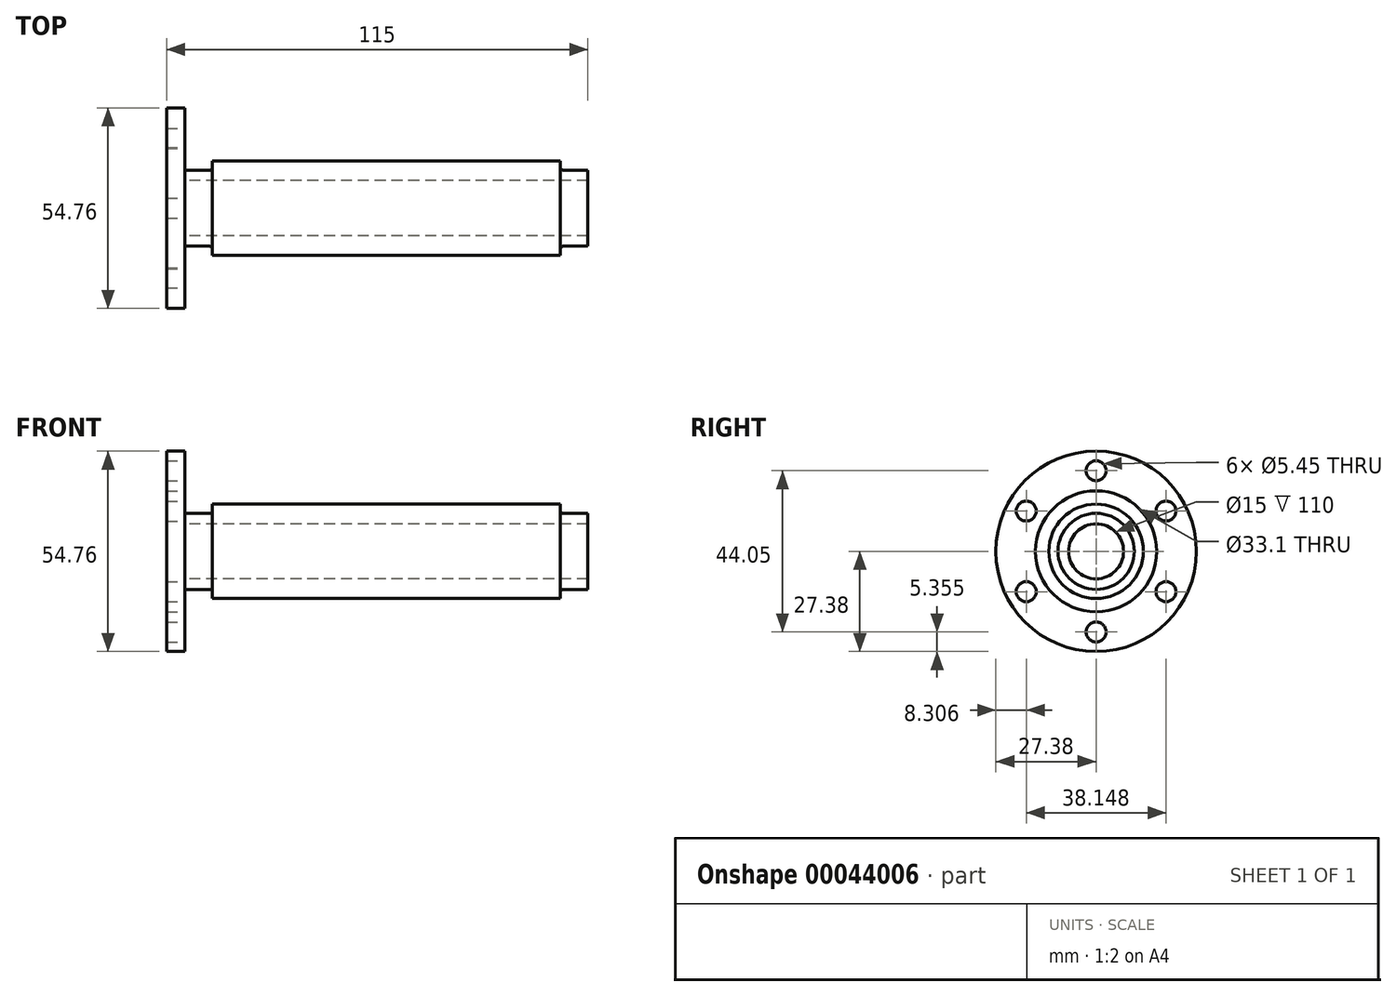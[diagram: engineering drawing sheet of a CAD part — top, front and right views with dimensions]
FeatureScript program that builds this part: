
annotation { "Feature Type Name" : "Feature", "Feature Type Description" : "" }
export const myFeature = defineFeature(function(context is Context, id is Id, definition is map)
    precondition{}
    {
        {
            var Q0;
            Q0=qCreatedBy(makeId("Front.planeOp"),FACE);
            var sketch = newSketch(context, id + "F0", { "sketchPlane" : qUnion([Q0])});
            skLineSegment(sketch, "E0", {"start": v(0, 0) * mm, "end": v(-45.87, 0) * mm});
            skLineSegment(sketch, "E1.0", {"start": v(0, 16.55) * mm, "end": v(-5, 16.55) * mm});
            skLineSegment(sketch, "E2.0", {"start": v(0, 27.38) * mm, "end": v(-5, 27.38) * mm});
            skLineSegment(sketch, "E3", {"start": v(0, 16.55) * mm, "end": v(0, 27.38) * mm});
            skLineSegment(sketch, "E4.0", {"start": v(-5, 16.55) * mm, "end": v(-5, 27.38) * mm});
            skSolve(sketch);
        }
        {
            var Q0;
            Q0=makeQuery(id+"F0.imprint","IMPRINT",FACE,{"disambiguationData":[TD([[makeQuery(id+"F0.imprint","IMPRINT",EDGE,{"derivedFrom":sQuery(id+"F0.wireOp",EDGE,"E1.0")}),-1.0]])]});
            var Q1;
            Q1=sQuery(id+"F0.wireOp",EDGE,"E0");
            revolve(context, id + "F1", {"entities" : qUnion([Q0]), "axis" : qUnion([Q1]), "revolveType" : RevolveType.FULL});
        }
        {
            var Q0;
            Q0=qCreatedBy(makeId("Right.planeOp"),FACE);
            var sketch = newSketch(context, id + "F2", { "sketchPlane" : qUnion([Q0])});
            skCircle(sketch, "E5", {"center": v(0, 22.02) * mm, "radius": 2.73 * mm});
            skCircle(sketch, "E6.1.0", {"center": v(-19.07, 11.01) * mm, "radius": 2.73 * mm});
            skCircle(sketch, "E6.2.0", {"center": v(-19.07, -11.01) * mm, "radius": 2.73 * mm});
            skCircle(sketch, "E6.3.0", {"center": v(0, -22.02) * mm, "radius": 2.73 * mm});
            skCircle(sketch, "E6.4.0", {"center": v(19.07, -11.01) * mm, "radius": 2.73 * mm});
            skCircle(sketch, "E6.5.0", {"center": v(19.07, 11.01) * mm, "radius": 2.73 * mm});
            skPoint(sketch, "E6.center", {"position": v(0, 0) * mm});
            skSolve(sketch);
        }
        {
            var Q0;
            Q0=makeQuery(id+"F2.imprint","IMPRINT",FACE,{"disambiguationData":[TD([[makeQuery(id+"F2.imprint","IMPRINT",EDGE,{"derivedFrom":sQuery(id+"F2.wireOp",EDGE,"E5")}),1.0]])]});
            var Q1;
            Q1=makeQuery(id+"F2.imprint","IMPRINT",FACE,{"disambiguationData":[TD([[makeQuery(id+"F2.imprint","IMPRINT",EDGE,{"derivedFrom":sQuery(id+"F2.wireOp",EDGE,"E6.1.0")}),1.0]])]});
            var Q2;
            Q2=makeQuery(id+"F2.imprint","IMPRINT",FACE,{"disambiguationData":[TD([[makeQuery(id+"F2.imprint","IMPRINT",EDGE,{"derivedFrom":sQuery(id+"F2.wireOp",EDGE,"E6.2.0")}),1.0]])]});
            var Q3;
            Q3=makeQuery(id+"F2.imprint","IMPRINT",FACE,{"disambiguationData":[TD([[makeQuery(id+"F2.imprint","IMPRINT",EDGE,{"derivedFrom":sQuery(id+"F2.wireOp",EDGE,"E6.3.0")}),1.0]])]});
            var Q4;
            Q4=makeQuery(id+"F2.imprint","IMPRINT",FACE,{"disambiguationData":[TD([[makeQuery(id+"F2.imprint","IMPRINT",EDGE,{"derivedFrom":sQuery(id+"F2.wireOp",EDGE,"E6.4.0")}),1.0]])]});
            var Q5;
            Q5=makeQuery(id+"F2.imprint","IMPRINT",FACE,{"disambiguationData":[TD([[makeQuery(id+"F2.imprint","IMPRINT",EDGE,{"derivedFrom":sQuery(id+"F2.wireOp",EDGE,"E6.5.0")}),1.0]])]});
            extrude(context, id + "F3", {"entities" : qUnion([Q0, Q1, Q2, Q3, Q4, Q5]), "operationType" : NewBodyOperationType.REMOVE, "oppositeDirection" : true, "depth" : 25 * mm});
        }
        {
            var Q0;
            Q0=qCreatedBy(makeId("Front.planeOp"),FACE);
            var sketch = newSketch(context, id + "F4", { "sketchPlane" : qUnion([Q0])});
            skLineSegment(sketch, "E7", {"start": v(6.15, 0) * mm, "end": v(138.41, 0) * mm});
            skLineSegment(sketch, "E8.bottom", {"start": v(0, 7.5) * mm, "end": v(110, 7.5) * mm});
            skLineSegment(sketch, "E8.top", {"start": v(7.5, 12.9) * mm, "end": v(102.5, 12.9) * mm});
            skLineSegment(sketch, "E8.left", {"start": v(0, 7.5) * mm, "end": v(0, 10.4) * mm});
            skLineSegment(sketch, "E8.right", {"start": v(110, 7.5) * mm, "end": v(110, 10.4) * mm});
            skLineSegment(sketch, "E9.0", {"start": v(0, 10.4) * mm, "end": v(6.75, 10.4) * mm});
            skLineSegment(sketch, "E10", {"start": v(102.5, 11.15) * mm, "end": v(102.5, 12.9) * mm});
            skLineSegment(sketch, "E11", {"start": v(7.5, 11.15) * mm, "end": v(7.5, 12.9) * mm});
            skLineSegment(sketch, "E12.trimOffspring", {"start": v(103.25, 10.4) * mm, "end": v(110, 10.4) * mm});
            skPoint(sketch, "E13.visualSharp", {"position": v(7.5, 10.4) * mm});
            skArc(sketch, "E13.filletArc", {"start": v(6.75, 10.4) * mm, "mid": v(7.28, 10.62) * mm, "end": v(7.5, 11.15) * mm});
            skPoint(sketch, "E14.visualSharp", {"position": v(102.5, 10.4) * mm});
            skArc(sketch, "E14.filletArc", {"start": v(102.5, 11.15) * mm, "mid": v(102.72, 10.62) * mm, "end": v(103.25, 10.4) * mm});
            skSolve(sketch);
        }
        {
            var Q0;
            Q0=makeQuery(id+"F4.imprint","IMPRINT",FACE,{"disambiguationData":[TD([[makeQuery(id+"F4.imprint","IMPRINT",EDGE,{"derivedFrom":sQuery(id+"F4.wireOp",EDGE,"E8.bottom")}),1.0]])]});
            var Q1;
            Q1=sQuery(id+"F4.wireOp",EDGE,"E7");
            revolve(context, id + "F5", {"entities" : qUnion([Q0]), "axis" : qUnion([Q1]), "revolveType" : RevolveType.FULL});
        }
    });
